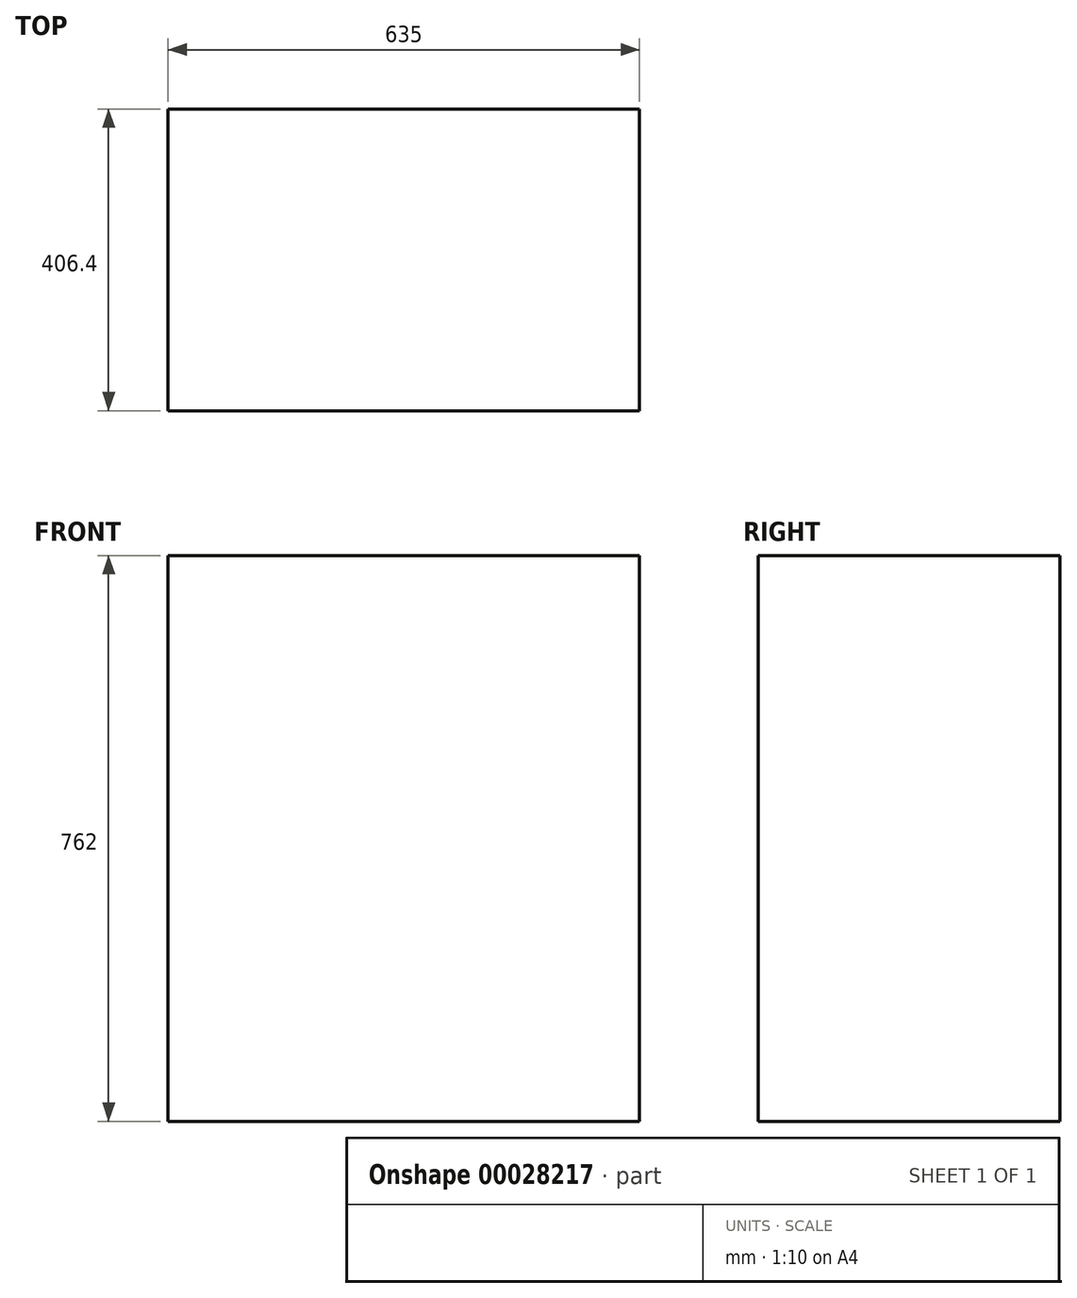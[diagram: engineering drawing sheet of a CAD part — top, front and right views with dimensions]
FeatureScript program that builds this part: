
annotation { "Feature Type Name" : "Feature", "Feature Type Description" : "" }
export const myFeature = defineFeature(function(context is Context, id is Id, definition is map)
    precondition{}
    {
        {
            var Q0;
            Q0=qCreatedBy(makeId("Top.planeOp"),FACE);
            var sketch = newSketch(context, id + "F0", { "sketchPlane" : qUnion([Q0])});
            skLineSegment(sketch, "E0.bottom", {"start": v(-308.52, 95.24) * mm, "end": v(326.48, 95.24) * mm});
            skLineSegment(sketch, "E0.top", {"start": v(-308.52, -311.16) * mm, "end": v(326.48, -311.16) * mm});
            skLineSegment(sketch, "E0.left", {"start": v(-308.52, 95.24) * mm, "end": v(-308.52, -311.16) * mm});
            skLineSegment(sketch, "E0.right", {"start": v(326.48, 95.24) * mm, "end": v(326.48, -311.16) * mm});
            skSolve(sketch);
        }
        {
            var Q0;
            Q0=makeQuery(id+"F0.imprint","IMPRINT",FACE,{"disambiguationData":[TD([[makeQuery(id+"F0.imprint","IMPRINT",EDGE,{"derivedFrom":sQuery(id+"F0.wireOp",EDGE,"E0.bottom")}),-1.0]])]});
            extrude(context, id + "F1", {"entities" : qUnion([Q0]), "depth" : 762 * mm});
        }
    });
